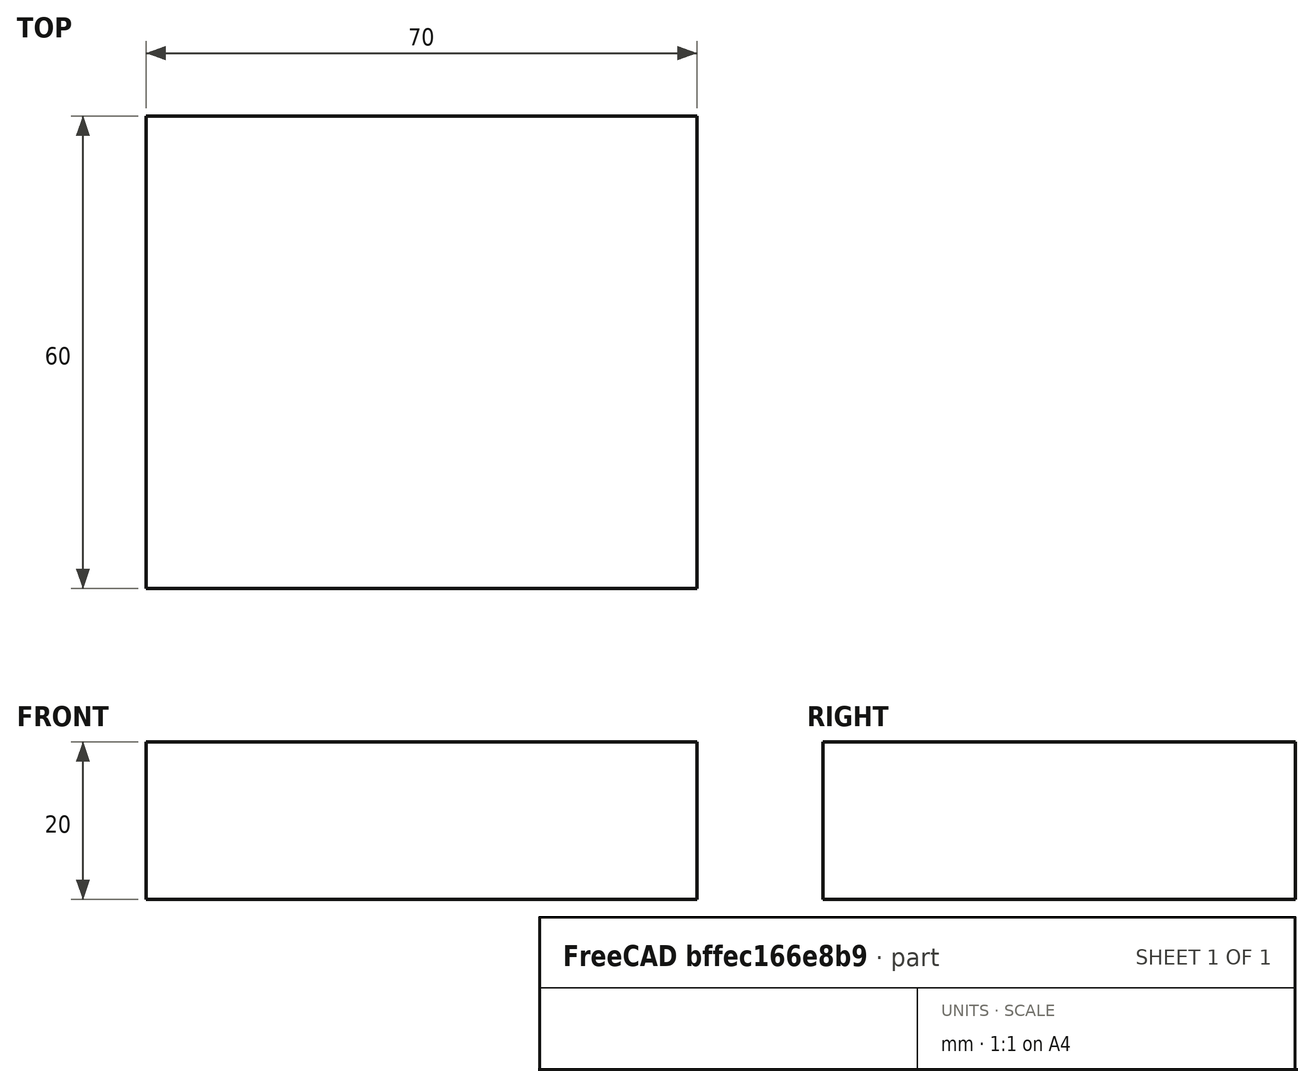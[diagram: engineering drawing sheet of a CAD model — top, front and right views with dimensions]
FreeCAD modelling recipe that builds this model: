
FCSTD DOCUMENT  (FreeCAD 0.21R33694 (Git))
Label: OJT1_T018_P01_rectangle_acotat
License: All rights reserved
LicenseURL: http://en.wikipedia.org/wiki/All_rights_reserved
objects: Sketcher::SketchObject×1, PartDesign::Pad×1, PartDesign::Body×1
note: 4 computed .brp shape members not serialized (recipe doc carries the construction recipe); baked Part::Feature solids carry a one-line shape summary decoded from their .brp

FEATURE [Sketcher::SketchObject] Sketch
  FullyConstrained = false
  MapMode = 5
  Support = -> [XY_Plane]
  sketch-geometry (8):
    g0: LineSegment StartX=-29.6837 StartY=40.0664 StartZ=0 EndX=40.3163 EndY=40.0664 EndZ=0
    g1: LineSegment StartX=-29.6837 StartY=40.0664 StartZ=0 EndX=-29.6837 EndY=-19.9336 EndZ=0
    g2: LineSegment StartX=-29.6837 StartY=-19.9336 StartZ=0 EndX=40.3163 EndY=-19.9336 EndZ=0
    g3: LineSegment StartX=40.3163 StartY=40.0664 StartZ=0 EndX=40.3163 EndY=-19.9336 EndZ=0
    g4: GeomPoint X=40.3163 Y=40.0664 Z=0
    g5: GeomPoint X=40.3163 Y=40.0664 Z=0
    g6: GeomPoint X=40.3163 Y=40.0664 Z=0
    g7: GeomPoint X=40.3163 Y=40.0664 Z=0
  constraints (14):
    c: Coincident(g4,g0)
    c: Coincident(g5,g3)
    c: Coincident(g6,g0)
    c: Coincident(g7,g3)
    c: Coincident(g0,g3)
    c: Coincident(g0,g1)
    c: Coincident(g2,g3)
    c: Coincident(g1,g2)
    c: Horizontal(g0)
    c: Horizontal(g2)
    c: Vertical(g1)
    c: Vertical(g3)
    c: DistanceY(g1,g1) = 60
    c: DistanceX(g0,g0) = 70
FEATURE [PartDesign::Pad] Pad
  Direction = (0,0,1)
  Length = 20
  Length2 = 10
  Profile = -> Sketch
  ReferenceAxis = -> Sketch [N_Axis]
  Type = 0
FEATURE [PartDesign::Body] Body
  Group = -> [Sketch,Pad]
  Origin = -> Origin
  Tip = -> Pad
